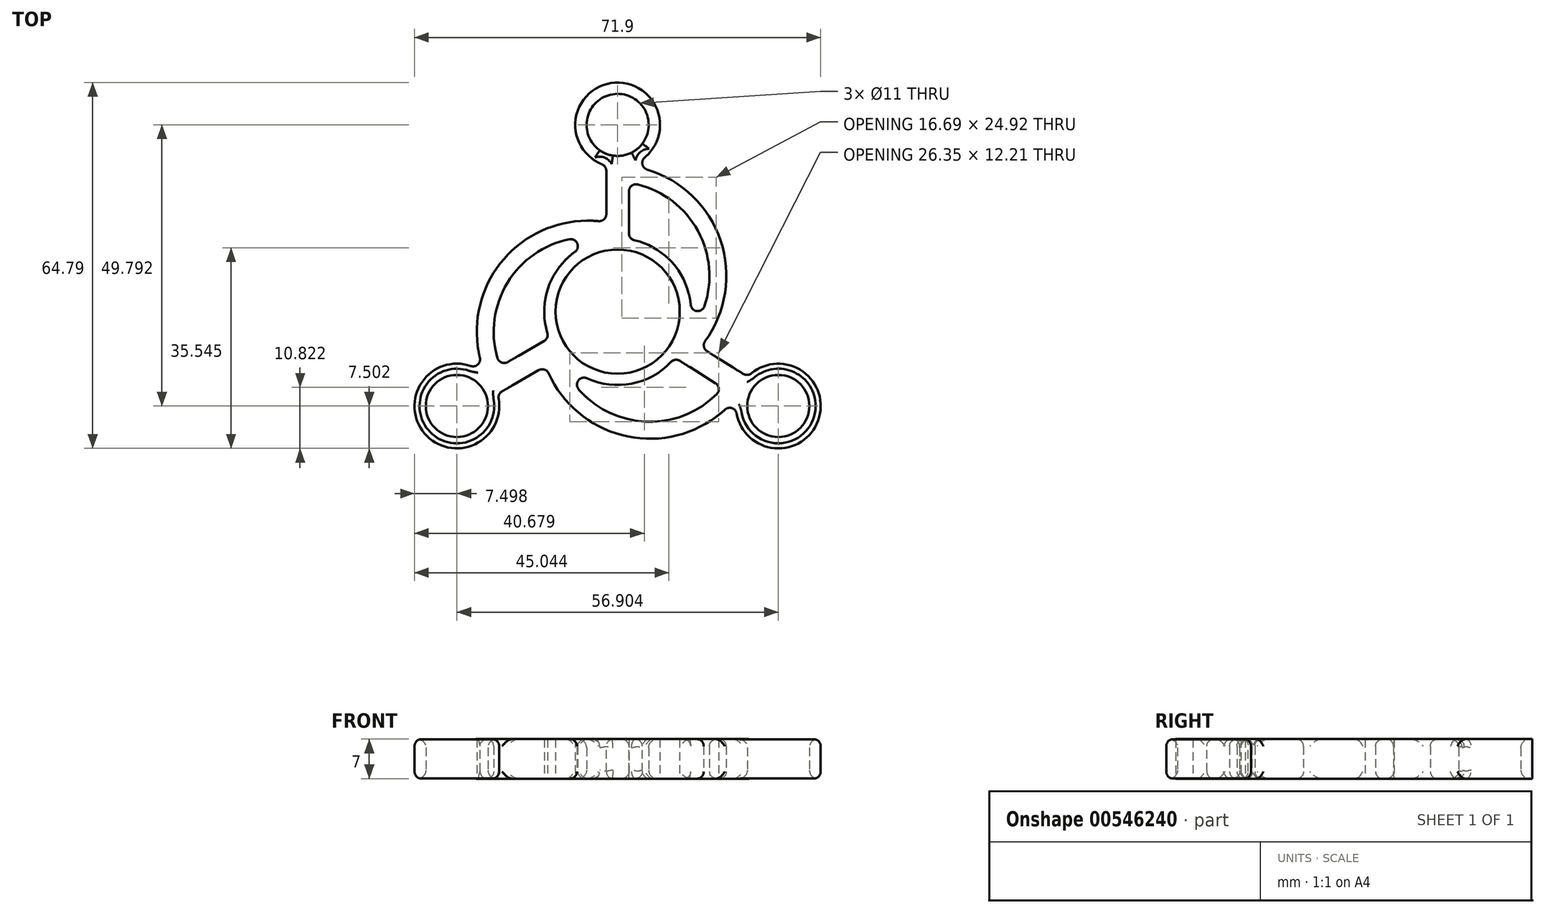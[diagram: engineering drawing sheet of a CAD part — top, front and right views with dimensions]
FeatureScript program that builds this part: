
annotation { "Feature Type Name" : "Feature", "Feature Type Description" : "" }
export const myFeature = defineFeature(function(context is Context, id is Id, definition is map)
    precondition{}
    {
        {
            var Q0;
            Q0=qCreatedBy(makeId("Top.planeOp"),FACE);
            var sketch = newSketch(context, id + "F0", { "sketchPlane" : qUnion([Q0])});
            skCircle(sketch, "E0", {"center": v(0, 0) * mm, "radius": 11 * mm});
            skCircle(sketch, "E1", {"center": v(0, 33.07) * mm, "radius": 5.5 * mm});
            skCircle(sketch, "E2", {"center": v(-28.45, -16.72) * mm, "radius": 5.5 * mm});
            skCircle(sketch, "E3", {"center": v(28.45, -16.72) * mm, "radius": 5.5 * mm});
            skCircle(sketch, "E4", {"center": v(0, 33.07) * mm, "radius": 7.5 * mm});
            skCircle(sketch, "E5", {"center": v(-28.45, -16.72) * mm, "radius": 7.5 * mm});
            skCircle(sketch, "E6", {"center": v(28.45, -16.72) * mm, "radius": 7.5 * mm});
            skCircle(sketch, "E7", {"center": v(0, 0) * mm, "radius": 13 * mm});
            skLineSegment(sketch, "E8", {"start": v(-12.12, -4.7) * mm, "end": v(-23.38, -11.2) * mm});
            skLineSegment(sketch, "E9", {"start": v(-10.12, -8.15) * mm, "end": v(-21.26, -14.58) * mm});
            skLineSegment(sketch, "E10", {"start": v(12.13, -4.69) * mm, "end": v(23.03, -11.53) * mm});
            skLineSegment(sketch, "E11", {"start": v(21.14, -15.06) * mm, "end": v(10.12, -8.15) * mm});
            skLineSegment(sketch, "E12", {"start": v(-2, 25.85) * mm, "end": v(-2, 12.85) * mm});
            skLineSegment(sketch, "E13", {"start": v(2, 25.85) * mm, "end": v(2, 12.85) * mm});
            skPoint(sketch, "E14", {"position": v(14.67, -6.28) * mm});
            skArc(sketch, "E15", {"start": v(14.67, -6.28) * mm, "mid": v(17.87, 13.54) * mm, "end": v(2, 25.85) * mm});
            skPoint(sketch, "E16", {"position": v(2, 22.82) * mm});
            skPoint(sketch, "E17", {"position": v(14.06, 14.58) * mm});
            skArc(sketch, "E18", {"start": v(12.13, -4.69) * mm, "mid": v(15.23, 12.07) * mm, "end": v(2, 22.82) * mm});
            skPoint(sketch, "E19", {"position": v(-2, 15.85) * mm});
            skPoint(sketch, "E20", {"position": v(-20.78, -9.7) * mm});
            skPoint(sketch, "E21", {"position": v(-17.46, 7.81) * mm});
            skArc(sketch, "E22", {"start": v(-2, 15.85) * mm, "mid": v(-20.69, 8.65) * mm, "end": v(-23.38, -11.2) * mm});
            skArc(sketch, "E23", {"start": v(-2, 12.85) * mm, "mid": v(-18.06, 7.13) * mm, "end": v(-20.78, -9.7) * mm});
            skPoint(sketch, "E24", {"position": v(-12.72, -9.65) * mm});
            skPoint(sketch, "E25", {"position": v(18.6, -13.47) * mm});
            skArc(sketch, "E26", {"start": v(-12.72, -9.65) * mm, "mid": v(2.62, -22.27) * mm, "end": v(21.14, -15.06) * mm});
            skPoint(sketch, "E27", {"position": v(4.58, -19.47) * mm});
            skArc(sketch, "E28", {"start": v(-10.12, -8.15) * mm, "mid": v(2.68, -19.23) * mm, "end": v(18.6, -13.47) * mm});
            skSolve(sketch);
        }
        {
            var Q0;
            Q0=qSketchRegion(id+"F0",true);
            var Q1;
            Q1=makeQuery(id+"F0.imprint","IMPRINT",FACE,{"disambiguationData":[TD([[makeQuery(id+"F0.imprint","IMPRINT",EDGE,{"derivedFrom":sQuery(id+"F0.wireOp",EDGE,"E0")}),-1.0]])]});
            var Q2;
            {var subQ0=sQuery(id+"F0.wireOp",EDGE,"E12");var subQ1=sQuery(id+"F0.wireOp",EDGE,"E7");var subQ2=makeQuery(id+"F0.imprint","INTERSECT",VERTEX,{"derivedFrom":[subQ1,subQ0]});Q2=makeQuery(id+"F0.imprint","IMPRINT",FACE,{"disambiguationData":[TD([[makeQuery(id+"F0.imprint","IMPRINT",EDGE,{"disambiguationData":[TD([[subQ2,1.0]])],"derivedFrom":subQ1}),-1.0]])]});}
            var Q3;
            {var subQ0=sQuery(id+"F0.wireOp",EDGE,"E8");var subQ1=sQuery(id+"F0.wireOp",EDGE,"E7");var subQ2=makeQuery(id+"F0.imprint","INTERSECT",VERTEX,{"derivedFrom":[subQ1,subQ0]});Q3=makeQuery(id+"F0.imprint","IMPRINT",FACE,{"disambiguationData":[TD([[makeQuery(id+"F0.imprint","IMPRINT",EDGE,{"disambiguationData":[TD([[subQ2,-1.0]])],"derivedFrom":subQ1}),-1.0]])]});}
            var Q4;
            {var subQ0=sQuery(id+"F0.wireOp",EDGE,"E10");var subQ1=sQuery(id+"F0.wireOp",EDGE,"E7");var subQ2=makeQuery(id+"F0.imprint","INTERSECT",VERTEX,{"derivedFrom":[subQ1,subQ0]});Q4=makeQuery(id+"F0.imprint","IMPRINT",FACE,{"disambiguationData":[TD([[makeQuery(id+"F0.imprint","IMPRINT",EDGE,{"disambiguationData":[TD([[subQ2,1.0]])],"derivedFrom":subQ1}),-1.0]])]});}
            extrude(context, id + "F1", {"entities" : qUnion([Q0, Q1, Q2, Q3, Q4]), "depth" : 7 * mm, "offsetDistance" : 25 * mm});
        }
        {
            var Q0;
            Q0=makeQuery(id+"F1.opExtrude","SWEPT_FACE",FACE,{"disambiguationData":[OSD([sQuery(id+"F0.wireOp",EDGE,"E23")])]});
            var Q1;
            Q1=makeQuery(id+"F1.opExtrude","SWEPT_FACE",FACE,{"disambiguationData":[OSD([sQuery(id+"F0.wireOp",EDGE,"E5")])]});
            var Q2;
            Q2=makeQuery(id+"F1.opExtrude","SWEPT_FACE",FACE,{"disambiguationData":[OSD([sQuery(id+"F0.wireOp",EDGE,"E6")])]});
            var Q3;
            Q3=makeQuery(id+"F1.opExtrude","SWEPT_FACE",FACE,{"disambiguationData":[OSD([sQuery(id+"F0.wireOp",EDGE,"E15")])]});
            var Q4;
            Q4=makeQuery(id+"F1.opExtrude","SWEPT_FACE",FACE,{"disambiguationData":[OSD([sQuery(id+"F0.wireOp",EDGE,"E12")])]});
            var Q5;
            Q5=makeQuery(id+"F1.opExtrude","SWEPT_FACE",FACE,{"disambiguationData":[OSD([sQuery(id+"F0.wireOp",EDGE,"E18")])]});
            var Q6;
            {var subQ0=sQuery(id+"F0.wireOp",EDGE,"E7");Q6=makeQuery(id+"F1.opExtrude","SWEPT_FACE",FACE,{"disambiguationData":[OSD([subQ0]),TDD([makeQuery(id+"F0.imprint","IMPRINT",EDGE,{"disambiguationData":[TD([[makeQuery(id+"F0.imprint","INTERSECT",VERTEX,{"derivedFrom":[subQ0,sQuery(id+"F0.wireOp",EDGE,"E11")]}),1.0]])],"derivedFrom":subQ0})])]});}
            var Q7;
            Q7=makeQuery(id+"F1.opExtrude","SWEPT_EDGE",EDGE,{"disambiguationData":[OSD([sQuery(id+"F0.wireOp",EDGE,"E9"),sQuery(id+"F0.wireOp",EDGE,"E26")])]});
            var Q8;
            Q8=makeQuery(id+"F1.opExtrude","SWEPT_EDGE",EDGE,{"disambiguationData":[OSD([sQuery(id+"F0.wireOp",EDGE,"E7"),sQuery(id+"F0.wireOp",EDGE,"E13")])]});
            var Q9;
            Q9=makeQuery(id+"F1.opExtrude","SWEPT_EDGE",EDGE,{"disambiguationData":[OSD([sQuery(id+"F0.wireOp",EDGE,"E11"),sQuery(id+"F0.wireOp",EDGE,"E28")])]});
            var Q10;
            Q10=makeQuery(id+"F1.opExtrude","SWEPT_EDGE",EDGE,{"disambiguationData":[OSD([sQuery(id+"F0.wireOp",EDGE,"E7"),sQuery(id+"F0.wireOp",EDGE,"E8")])]});
            fillet(context, id + "F2", {"entities" : qUnion([Q0, Q1, Q2, Q3, Q4, Q5, Q6, Q7, Q8, Q9, Q10]), "radius" : 1.25 * mm, "tangentPropagation" : true, "allowEdgeOverflow" : false});
        }
        {
            var Q0;
            Q0=makeQuery(id+"F1.opExtrude","CAP_EDGE",EDGE,{"disambiguationData":[OSD([sQuery(id+"F0.wireOp",EDGE,"E2")])],"isStart":false});
            var Q1;
            Q1=makeQuery(id+"F1.opExtrude","CAP_EDGE",EDGE,{"disambiguationData":[OSD([sQuery(id+"F0.wireOp",EDGE,"E1")])],"isStart":false});
            var Q2;
            Q2=makeQuery(id+"F1.opExtrude","CAP_EDGE",EDGE,{"disambiguationData":[OSD([sQuery(id+"F0.wireOp",EDGE,"E3")])],"isStart":false});
            fillet(context, id + "F3", {"entities" : qUnion([Q0, Q1, Q2]), "radius" : 1.5 * mm, "tangentPropagation" : true, "allowEdgeOverflow" : false});
        }
        {
            var Q0;
            Q0=makeQuery(id+"F1.opExtrude","CAP_EDGE",EDGE,{"disambiguationData":[OSD([sQuery(id+"F0.wireOp",EDGE,"E1")])],"isStart":true});
            var Q1;
            Q1=makeQuery(id+"F1.opExtrude","CAP_EDGE",EDGE,{"disambiguationData":[OSD([sQuery(id+"F0.wireOp",EDGE,"E3")])],"isStart":true});
            var Q2;
            Q2=makeQuery(id+"F1.opExtrude","CAP_EDGE",EDGE,{"disambiguationData":[OSD([sQuery(id+"F0.wireOp",EDGE,"E2")])],"isStart":true});
            fillet(context, id + "F4", {"entities" : qUnion([Q0, Q1, Q2]), "radius" : 1.5 * mm, "tangentPropagation" : true, "allowEdgeOverflow" : false});
        }
    });
